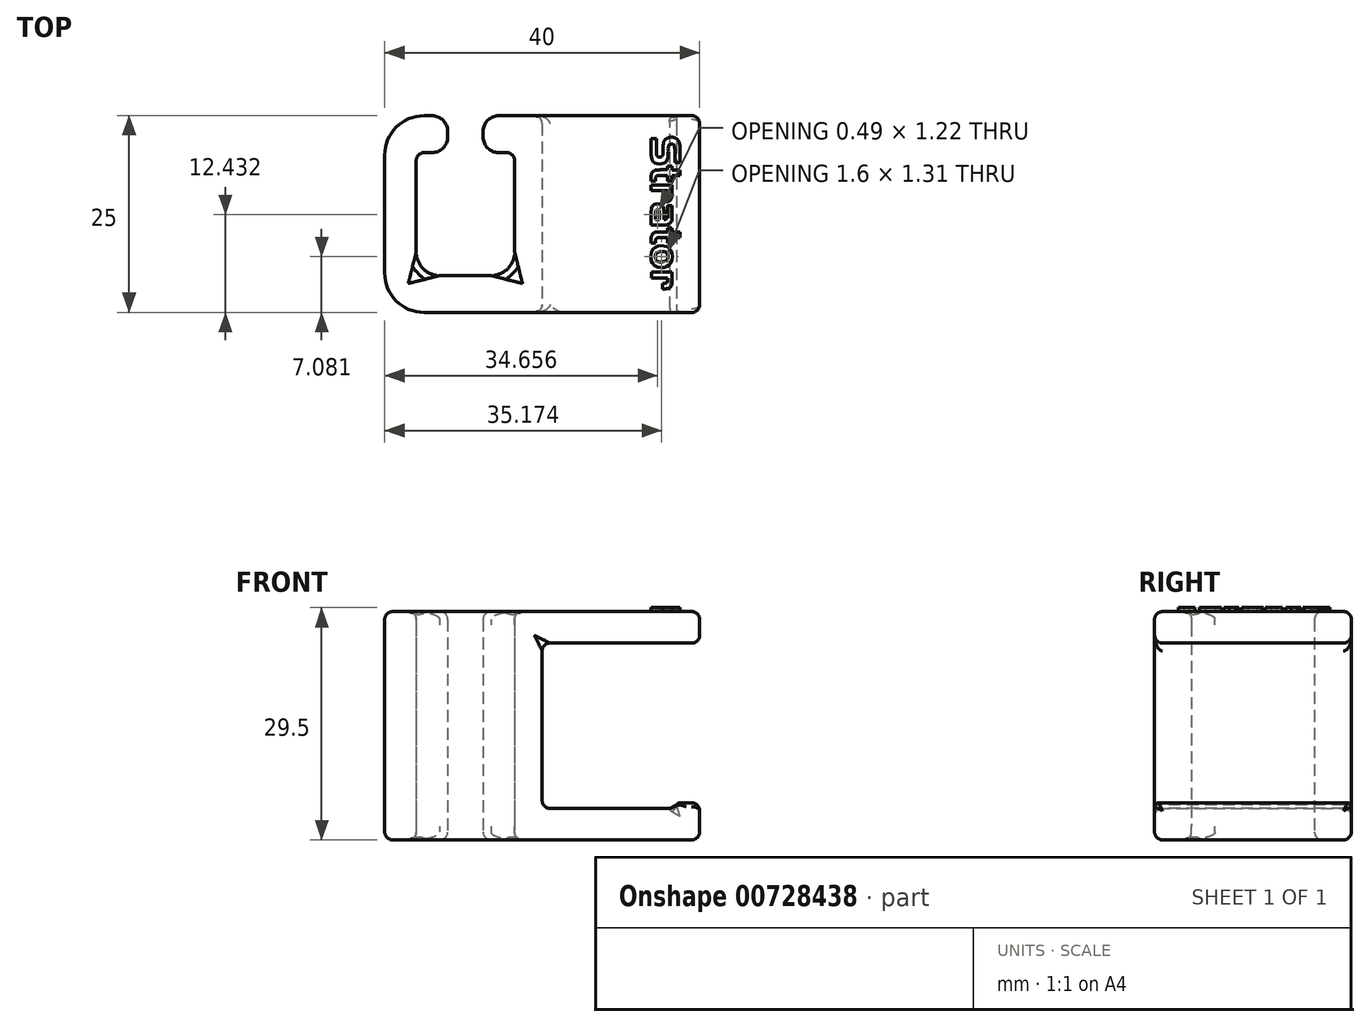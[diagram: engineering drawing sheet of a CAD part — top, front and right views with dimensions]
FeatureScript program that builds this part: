
annotation { "Feature Type Name" : "Feature", "Feature Type Description" : "" }
export const myFeature = defineFeature(function(context is Context, id is Id, definition is map)
    precondition{}
    {
        {
            var Q0;
            Q0=qCreatedBy(makeId("Top.planeOp"),FACE);
            var sketch = newSketch(context, id + "F0", { "sketchPlane" : qUnion([Q0])});
            skLineSegment(sketch, "E0", {"start": v(20, 11.92) * mm, "end": v(20, -13.08) * mm});
            skLineSegment(sketch, "E1", {"start": v(20, -13.08) * mm, "end": v(-20, -13.08) * mm});
            skLineSegment(sketch, "E2", {"start": v(-20, -13.08) * mm, "end": v(-20, 11.92) * mm});
            skLineSegment(sketch, "E3", {"start": v(-20, 11.92) * mm, "end": v(-12, 11.92) * mm});
            skLineSegment(sketch, "E4", {"start": v(-12, 11.92) * mm, "end": v(-12, 7.23) * mm});
            skLineSegment(sketch, "E5", {"start": v(-12, 7.23) * mm, "end": v(-16, 7.23) * mm});
            skLineSegment(sketch, "E6", {"start": v(-16, 7.23) * mm, "end": v(-16, -8.4) * mm});
            skLineSegment(sketch, "E7", {"start": v(-16, -8.4) * mm, "end": v(-3.5, -8.4) * mm});
            skLineSegment(sketch, "E8", {"start": v(-3.5, -8.4) * mm, "end": v(-3.5, 7.23) * mm});
            skLineSegment(sketch, "E9", {"start": v(-3.5, 7.23) * mm, "end": v(-7.5, 7.23) * mm});
            skLineSegment(sketch, "E10", {"start": v(-7.5, 7.23) * mm, "end": v(-7.5, 11.92) * mm});
            skLineSegment(sketch, "E11", {"start": v(-7.5, 11.92) * mm, "end": v(20, 11.92) * mm});
            skSolve(sketch);
        }
        {
            var Q0;
            Q0=makeQuery(id+"F0.imprint","IMPRINT",FACE,{"disambiguationData":[TD([[makeQuery(id+"F0.imprint","IMPRINT",EDGE,{"derivedFrom":sQuery(id+"F0.wireOp",EDGE,"E0")}),-1.0]])]});
            extrude(context, id + "F1", {"entities" : qUnion([Q0]), "depth" : 29 * mm, "offsetDistance" : 25 * mm});
        }
        {
            var Q0;
            Q0=qCreatedBy(makeId("Front.planeOp"),FACE);
            var sketch = newSketch(context, id + "F2", { "sketchPlane" : qUnion([Q0])});
            skLineSegment(sketch, "E12", {"start": v(0, 4) * mm, "end": v(0, 25) * mm});
            skLineSegment(sketch, "E13", {"start": v(0, 25) * mm, "end": v(36.44, 25) * mm});
            skLineSegment(sketch, "E14", {"start": v(36.44, 25) * mm, "end": v(36.44, 4.7) * mm});
            skLineSegment(sketch, "E15", {"start": v(36.44, 4.7) * mm, "end": v(17, 4.7) * mm});
            skLineSegment(sketch, "E16", {"start": v(17, 4.7) * mm, "end": v(17, 4) * mm});
            skLineSegment(sketch, "E17", {"start": v(17, 4) * mm, "end": v(0, 4) * mm});
            skLineSegment(sketch, "E18", {"start": v(26.72, 0) * mm, "end": v(26.72, 29) * mm, "construction": true});
            skPoint(sketch, "E18.startSnap0", {"position": v(26.72, 4.7) * mm});
            skSolve(sketch);
        }
        {
            var Q0;
            Q0=makeQuery(id+"F2.imprint","IMPRINT",FACE,{"disambiguationData":[TD([[makeQuery(id+"F2.imprint","IMPRINT",EDGE,{"derivedFrom":sQuery(id+"F2.wireOp",EDGE,"E12")}),-1.0]])]});
            extrude(context, id + "F3", {"entities" : qUnion([Q0]), "operationType" : NewBodyOperationType.REMOVE, "endBound" : BoundingType.THROUGH_ALL, "oppositeDirection" : true, "depth" : 25 * mm, "offsetDistance" : 25 * mm, "hasSecondDirection" : true, "secondDirectionOppositeDirection" : false, "secondDirectionDepth" : 25 * mm});
        }
        {
            var Q0;
            Q0=makeQuery(id+"F1.opExtrude","CAP_FACE",FACE,{"disambiguationData":[OSD([sQuery(id+"F0.wireOp",EDGE,"E0"),sQuery(id+"F0.wireOp",EDGE,"E1"),sQuery(id+"F0.wireOp",EDGE,"E2"),sQuery(id+"F0.wireOp",EDGE,"E3"),sQuery(id+"F0.wireOp",EDGE,"E4"),sQuery(id+"F0.wireOp",EDGE,"E5"),sQuery(id+"F0.wireOp",EDGE,"E6"),sQuery(id+"F0.wireOp",EDGE,"E7"),sQuery(id+"F0.wireOp",EDGE,"E8"),sQuery(id+"F0.wireOp",EDGE,"E9"),sQuery(id+"F0.wireOp",EDGE,"E10"),sQuery(id+"F0.wireOp",EDGE,"E11")])],"isStart":false});
            var Q1;
            Q1=makeQuery(id+"F1.opExtrude","SWEPT_EDGE",EDGE,{"disambiguationData":[OSD([sQuery(id+"F0.wireOp",EDGE,"E8"),sQuery(id+"F0.wireOp",EDGE,"E9")])]});
            var Q2;
            Q2=makeQuery(id+"F1.opExtrude","SWEPT_EDGE",EDGE,{"disambiguationData":[OSD([sQuery(id+"F0.wireOp",EDGE,"E5"),sQuery(id+"F0.wireOp",EDGE,"E6")])]});
            var Q3;
            Q3=makeQuery(id+"F1.opExtrude","CAP_EDGE",EDGE,{"disambiguationData":[OSD([sQuery(id+"F0.wireOp",EDGE,"E8")])],"isStart":true});
            var Q4;
            Q4=makeQuery(id+"F1.opExtrude","CAP_FACE",FACE,{"disambiguationData":[OSD([sQuery(id+"F0.wireOp",EDGE,"E0"),sQuery(id+"F0.wireOp",EDGE,"E1"),sQuery(id+"F0.wireOp",EDGE,"E2"),sQuery(id+"F0.wireOp",EDGE,"E3"),sQuery(id+"F0.wireOp",EDGE,"E4"),sQuery(id+"F0.wireOp",EDGE,"E5"),sQuery(id+"F0.wireOp",EDGE,"E6"),sQuery(id+"F0.wireOp",EDGE,"E7"),sQuery(id+"F0.wireOp",EDGE,"E8"),sQuery(id+"F0.wireOp",EDGE,"E9"),sQuery(id+"F0.wireOp",EDGE,"E10"),sQuery(id+"F0.wireOp",EDGE,"E11")])],"isStart":true});
            var Q5;
            Q5=makeQuery(id+"F3.boolean.opBoolean","INTERSECT",EDGE,{"derivedFrom":[makeQuery(id+"F1.opExtrude","SWEPT_FACE",FACE,{"disambiguationData":[OSD([sQuery(id+"F0.wireOp",EDGE,"E0")])]}),makeQuery(id+"F3.opExtrude","SWEPT_FACE",FACE,{"disambiguationData":[OSD([sQuery(id+"F2.wireOp",EDGE,"E15")])]})]});
            var Q6;
            Q6=makeQuery(id+"F3.boolean.opBoolean","INTERSECT",EDGE,{"derivedFrom":[makeQuery(id+"F1.opExtrude","SWEPT_FACE",FACE,{"disambiguationData":[OSD([sQuery(id+"F0.wireOp",EDGE,"E0")])]}),makeQuery(id+"F3.opExtrude","SWEPT_FACE",FACE,{"disambiguationData":[OSD([sQuery(id+"F2.wireOp",EDGE,"E13")])]})]});
            var Q7;
            Q7=makeQuery(id+"F3.boolean.opBoolean","INTERSECT",EDGE,{"derivedFrom":[makeQuery(id+"F1.opExtrude","SWEPT_FACE",FACE,{"disambiguationData":[OSD([sQuery(id+"F0.wireOp",EDGE,"E11")])]}),makeQuery(id+"F3.opExtrude","SWEPT_FACE",FACE,{"disambiguationData":[OSD([sQuery(id+"F2.wireOp",EDGE,"E13")])]})]});
            var Q8;
            {var subQ0=sQuery(id+"F0.wireOp",EDGE,"E0");var subQ1=sQuery(id+"F0.wireOp",EDGE,"E1");Q8=makeQuery(id+"F3.boolean.opBoolean","SPLIT",EDGE,{"disambiguationData":[TD([makeQuery(id+"F3.opExtrude","SWEPT_FACE",FACE,{"disambiguationData":[OSD([sQuery(id+"F2.wireOp",EDGE,"E15")])]})])],"derivedFrom":makeQuery(id+"F1.opExtrude","SWEPT_EDGE",EDGE,{"disambiguationData":[OSD([subQ0,subQ1])]})});}
            var Q9;
            Q9=makeQuery(id+"F3.boolean.opBoolean","COPY",EDGE,{"derivedFrom":makeQuery(id+"F3.opExtrude","SWEPT_EDGE",EDGE,{"disambiguationData":[OSD([sQuery(id+"F2.wireOp",EDGE,"E12"),sQuery(id+"F2.wireOp",EDGE,"E17")])]})});
            var Q10;
            Q10=makeQuery(id+"F3.boolean.opBoolean","INTERSECT",EDGE,{"derivedFrom":[makeQuery(id+"F1.opExtrude","SWEPT_FACE",FACE,{"disambiguationData":[OSD([sQuery(id+"F0.wireOp",EDGE,"E1")])]}),makeQuery(id+"F3.opExtrude","SWEPT_FACE",FACE,{"disambiguationData":[OSD([sQuery(id+"F2.wireOp",EDGE,"E13")])]})]});
            var Q11;
            Q11=makeQuery(id+"F3.boolean.opBoolean","INTERSECT",EDGE,{"derivedFrom":[makeQuery(id+"F1.opExtrude","SWEPT_FACE",FACE,{"disambiguationData":[OSD([sQuery(id+"F0.wireOp",EDGE,"E1")])]}),makeQuery(id+"F3.opExtrude","SWEPT_FACE",FACE,{"disambiguationData":[OSD([sQuery(id+"F2.wireOp",EDGE,"E12")])]})]});
            var Q12;
            {var subQ0=sQuery(id+"F0.wireOp",EDGE,"E0");var subQ1=sQuery(id+"F0.wireOp",EDGE,"E11");Q12=makeQuery(id+"F3.boolean.opBoolean","SPLIT",EDGE,{"disambiguationData":[TD([makeQuery(id+"F3.opExtrude","SWEPT_FACE",FACE,{"disambiguationData":[OSD([sQuery(id+"F2.wireOp",EDGE,"E15")])]})])],"derivedFrom":makeQuery(id+"F1.opExtrude","SWEPT_EDGE",EDGE,{"disambiguationData":[OSD([subQ0,subQ1])]})});}
            fillet(context, id + "F4", {"entities" : qUnion([Q0, Q1, Q2, Q3, Q4, Q5, Q6, Q7, Q8, Q9, Q10, Q11, Q12]), "radius" : 1 * mm, "tangentPropagation" : true, "allowEdgeOverflow" : false});
        }
        {
            var Q0;
            Q0=makeQuery(id+"F3.boolean.opBoolean","INTERSECT",EDGE,{"derivedFrom":[makeQuery(id+"F1.opExtrude","SWEPT_FACE",FACE,{"disambiguationData":[OSD([sQuery(id+"F0.wireOp",EDGE,"E11")])]}),makeQuery(id+"F3.opExtrude","SWEPT_FACE",FACE,{"disambiguationData":[OSD([sQuery(id+"F2.wireOp",EDGE,"E12")])]})]});
            fillet(context, id + "F5", {"entities" : qUnion([Q0]), "radius" : 1 * mm, "tangentPropagation" : true, "allowEdgeOverflow" : false});
        }
        {
            var Q0;
            Q0=makeQuery(id+"F3.boolean.opBoolean","COPY",EDGE,{"derivedFrom":makeQuery(id+"F3.opExtrude","SWEPT_EDGE",EDGE,{"disambiguationData":[OSD([sQuery(id+"F2.wireOp",EDGE,"E15"),sQuery(id+"F2.wireOp",EDGE,"E16")])]})});
            var Q1;
            Q1=makeQuery(id+"F3.boolean.opBoolean","INTERSECT",EDGE,{"derivedFrom":[makeQuery(id+"F1.opExtrude","SWEPT_FACE",FACE,{"disambiguationData":[OSD([sQuery(id+"F0.wireOp",EDGE,"E11")])]}),makeQuery(id+"F3.opExtrude","SWEPT_FACE",FACE,{"disambiguationData":[OSD([sQuery(id+"F2.wireOp",EDGE,"E15")])]})]});
            var Q2;
            Q2=makeQuery(id+"F3.boolean.opBoolean","INTERSECT",EDGE,{"derivedFrom":[makeQuery(id+"F1.opExtrude","SWEPT_FACE",FACE,{"disambiguationData":[OSD([sQuery(id+"F0.wireOp",EDGE,"E1")])]}),makeQuery(id+"F3.opExtrude","SWEPT_FACE",FACE,{"disambiguationData":[OSD([sQuery(id+"F2.wireOp",EDGE,"E15")])]})]});
            var Q3;
            Q3=makeQuery(id+"F3.boolean.opBoolean","INTERSECT",EDGE,{"derivedFrom":[makeQuery(id+"F1.opExtrude","SWEPT_FACE",FACE,{"disambiguationData":[OSD([sQuery(id+"F0.wireOp",EDGE,"E1")])]}),makeQuery(id+"F3.opExtrude","SWEPT_FACE",FACE,{"disambiguationData":[OSD([sQuery(id+"F2.wireOp",EDGE,"E16")])]})]});
            var Q4;
            Q4=makeQuery(id+"F3.boolean.opBoolean","INTERSECT",EDGE,{"derivedFrom":[makeQuery(id+"F1.opExtrude","SWEPT_FACE",FACE,{"disambiguationData":[OSD([sQuery(id+"F0.wireOp",EDGE,"E11")])]}),makeQuery(id+"F3.opExtrude","SWEPT_FACE",FACE,{"disambiguationData":[OSD([sQuery(id+"F2.wireOp",EDGE,"E16")])]})]});
            fillet(context, id + "F6", {"entities" : qUnion([Q0, Q1, Q2, Q3, Q4]), "radius" : 0.5 * mm, "tangentPropagation" : true, "allowEdgeOverflow" : false});
        }
        {
            var Q0;
            {var subQ0=sQuery(id+"F2.wireOp",EDGE,"E16");Q0=makeQuery(id+"F6.opFillet","BLEND_EDGE",EDGE,{"blendedFrom":[makeQuery(id+"F3.boolean.opBoolean","COPY",EDGE,{"derivedFrom":makeQuery(id+"F3.opExtrude","SWEPT_EDGE",EDGE,{"disambiguationData":[OSD([sQuery(id+"F2.wireOp",EDGE,"E15"),subQ0])]})}),makeQuery(id+"F3.boolean.opBoolean","COPY",FACE,{"derivedFrom":makeQuery(id+"F3.opExtrude","SWEPT_FACE",FACE,{"disambiguationData":[OSD([subQ0])]})})],"blendedInto":[makeQuery(id+"F3.boolean.opBoolean","COPY",FACE,{"derivedFrom":makeQuery(id+"F3.opExtrude","SWEPT_FACE",FACE,{"disambiguationData":[OSD([subQ0])]})})]});}
            var Q1;
            Q1=makeQuery(id+"F3.boolean.opBoolean","COPY",EDGE,{"derivedFrom":makeQuery(id+"F3.opExtrude","SWEPT_EDGE",EDGE,{"disambiguationData":[OSD([sQuery(id+"F2.wireOp",EDGE,"E16"),sQuery(id+"F2.wireOp",EDGE,"E17")])]})});
            chamfer(context, id + "F7", {"entities" : qUnion([Q0, Q1]), "width" : 1 * mm, "tangentPropagation" : true});
        }
        {
            var Q0;
            Q0=makeQuery(id+"F1.opExtrude","SWEPT_EDGE",EDGE,{"disambiguationData":[OSD([sQuery(id+"F0.wireOp",EDGE,"E1"),sQuery(id+"F0.wireOp",EDGE,"E2")])]});
            fillet(context, id + "F8", {"entities" : qUnion([Q0]), "radius" : 5 * mm, "tangentPropagation" : true, "allowEdgeOverflow" : false});
        }
        {
            var Q0;
            Q0=makeQuery(id+"F1.opExtrude","SWEPT_EDGE",EDGE,{"disambiguationData":[OSD([sQuery(id+"F0.wireOp",EDGE,"E2"),sQuery(id+"F0.wireOp",EDGE,"E3")])]});
            fillet(context, id + "F9", {"entities" : qUnion([Q0]), "radius" : 5 * mm, "tangentPropagation" : true, "allowEdgeOverflow" : false});
        }
        {
            var Q0;
            Q0=makeQuery(id+"F1.opExtrude","SWEPT_EDGE",EDGE,{"disambiguationData":[OSD([sQuery(id+"F0.wireOp",EDGE,"E7"),sQuery(id+"F0.wireOp",EDGE,"E8")])]});
            var Q1;
            Q1=makeQuery(id+"F1.opExtrude","SWEPT_EDGE",EDGE,{"disambiguationData":[OSD([sQuery(id+"F0.wireOp",EDGE,"E6"),sQuery(id+"F0.wireOp",EDGE,"E7")])]});
            fillet(context, id + "F10", {"entities" : qUnion([Q0, Q1]), "radius" : 3 * mm, "tangentPropagation" : true, "allowEdgeOverflow" : false});
        }
        {
            var Q0;
            Q0=makeQuery(id+"F3.boolean.opBoolean","COPY",FACE,{"derivedFrom":makeQuery(id+"F3.opExtrude","SWEPT_FACE",FACE,{"disambiguationData":[OSD([sQuery(id+"F2.wireOp",EDGE,"E13")])]})});
            fillet(context, id + "F11", {"entities" : qUnion([Q0]), "radius" : 1 * mm, "tangentPropagation" : true, "allowEdgeOverflow" : false});
        }
        {
            var Q0;
            {var subQ0=sQuery(id+"F0.wireOp",EDGE,"E0");var subQ1=sQuery(id+"F0.wireOp",EDGE,"E11");Q0=makeQuery(id+"F3.boolean.opBoolean","SPLIT",EDGE,{"disambiguationData":[TD([makeQuery(id+"F3.opExtrude","SWEPT_FACE",FACE,{"disambiguationData":[OSD([sQuery(id+"F2.wireOp",EDGE,"E13")])]})])],"derivedFrom":makeQuery(id+"F1.opExtrude","SWEPT_EDGE",EDGE,{"disambiguationData":[OSD([subQ0,subQ1])]})});}
            var Q1;
            {var subQ0=sQuery(id+"F0.wireOp",EDGE,"E0");var subQ1=sQuery(id+"F0.wireOp",EDGE,"E1");Q1=makeQuery(id+"F3.boolean.opBoolean","SPLIT",EDGE,{"disambiguationData":[TD([makeQuery(id+"F3.opExtrude","SWEPT_FACE",FACE,{"disambiguationData":[OSD([sQuery(id+"F2.wireOp",EDGE,"E13")])]})])],"derivedFrom":makeQuery(id+"F1.opExtrude","SWEPT_EDGE",EDGE,{"disambiguationData":[OSD([subQ0,subQ1])]})});}
            fillet(context, id + "F12", {"entities" : qUnion([Q0, Q1]), "radius" : 1 * mm, "tangentPropagation" : true, "allowEdgeOverflow" : false});
        }
        {
            var Q0;
            Q0=makeQuery(id+"F1.opExtrude","SWEPT_EDGE",EDGE,{"disambiguationData":[OSD([sQuery(id+"F0.wireOp",EDGE,"E9"),sQuery(id+"F0.wireOp",EDGE,"E10")])]});
            var Q1;
            Q1=makeQuery(id+"F1.opExtrude","SWEPT_EDGE",EDGE,{"disambiguationData":[OSD([sQuery(id+"F0.wireOp",EDGE,"E10"),sQuery(id+"F0.wireOp",EDGE,"E11")])]});
            var Q2;
            Q2=makeQuery(id+"F1.opExtrude","SWEPT_EDGE",EDGE,{"disambiguationData":[OSD([sQuery(id+"F0.wireOp",EDGE,"E3"),sQuery(id+"F0.wireOp",EDGE,"E4")])]});
            var Q3;
            Q3=makeQuery(id+"F1.opExtrude","SWEPT_EDGE",EDGE,{"disambiguationData":[OSD([sQuery(id+"F0.wireOp",EDGE,"E4"),sQuery(id+"F0.wireOp",EDGE,"E5")])]});
            fillet(context, id + "F13", {"entities" : qUnion([Q0, Q1, Q2, Q3]), "radius" : 2 * mm, "tangentPropagation" : true, "allowEdgeOverflow" : false});
        }
        {
            var Q0;
            Q0=qCreatedBy(makeId("Top.planeOp"),FACE);
            var sketch = newSketch(context, id + "F14", { "sketchPlane" : qUnion([Q0])});
            skLineSegment(sketch, "E19", {"start": v(22.35, 9) * mm, "end": v(23, 9) * mm});
            skLineSegment(sketch, "E20", {"start": v(23, 9) * mm, "end": v(23, 7.12) * mm});
            skLineSegment(sketch, "E21", {"start": v(23, 7.12) * mm, "end": v(23.03, 6.93) * mm});
            skLineSegment(sketch, "E22", {"start": v(23.03, 6.93) * mm, "end": v(23.06, 6.83) * mm});
            skLineSegment(sketch, "E23", {"start": v(23.06, 6.83) * mm, "end": v(23.1, 6.78) * mm});
            skLineSegment(sketch, "E24", {"start": v(23.1, 6.78) * mm, "end": v(23.12, 6.76) * mm});
            skLineSegment(sketch, "E25", {"start": v(23.12, 6.76) * mm, "end": v(23.15, 6.73) * mm});
            skLineSegment(sketch, "E26", {"start": v(23.15, 6.73) * mm, "end": v(23.2, 6.69) * mm});
            skLineSegment(sketch, "E27", {"start": v(23.2, 6.69) * mm, "end": v(23.25, 6.66) * mm});
            skLineSegment(sketch, "E28", {"start": v(23.25, 6.66) * mm, "end": v(23.32, 6.64) * mm});
            skLineSegment(sketch, "E29", {"start": v(23.32, 6.64) * mm, "end": v(23.4, 6.63) * mm});
            skLineSegment(sketch, "E30", {"start": v(23.4, 6.63) * mm, "end": v(23.47, 6.63) * mm});
            skLineSegment(sketch, "E31", {"start": v(23.47, 6.63) * mm, "end": v(23.53, 6.64) * mm});
            skLineSegment(sketch, "E32", {"start": v(23.53, 6.64) * mm, "end": v(23.62, 6.68) * mm});
            skLineSegment(sketch, "E33", {"start": v(23.62, 6.68) * mm, "end": v(23.68, 6.72) * mm});
            skLineSegment(sketch, "E34", {"start": v(23.68, 6.72) * mm, "end": v(23.71, 6.75) * mm});
            skLineSegment(sketch, "E35", {"start": v(23.71, 6.75) * mm, "end": v(23.75, 6.79) * mm});
            skLineSegment(sketch, "E36", {"start": v(23.75, 6.79) * mm, "end": v(23.79, 6.83) * mm});
            skLineSegment(sketch, "E37", {"start": v(23.79, 6.83) * mm, "end": v(23.82, 6.9) * mm});
            skLineSegment(sketch, "E38", {"start": v(23.82, 6.9) * mm, "end": v(23.84, 6.98) * mm});
            skLineSegment(sketch, "E39", {"start": v(23.84, 6.98) * mm, "end": v(23.86, 7.05) * mm});
            skLineSegment(sketch, "E40", {"start": v(23.86, 7.05) * mm, "end": v(23.87, 7.1) * mm});
            skLineSegment(sketch, "E41", {"start": v(23.87, 7.1) * mm, "end": v(23.88, 7.26) * mm});
            skLineSegment(sketch, "E42", {"start": v(23.88, 7.26) * mm, "end": v(23.88, 7.52) * mm});
            skLineSegment(sketch, "E43", {"start": v(23.88, 7.52) * mm, "end": v(23.88, 8.08) * mm});
            skLineSegment(sketch, "E44", {"start": v(23.88, 8.08) * mm, "end": v(23.88, 8.16) * mm});
            skLineSegment(sketch, "E45", {"start": v(23.88, 8.16) * mm, "end": v(23.9, 8.3) * mm});
            skLineSegment(sketch, "E46", {"start": v(23.9, 8.3) * mm, "end": v(23.9, 8.4) * mm});
            skLineSegment(sketch, "E47", {"start": v(23.9, 8.4) * mm, "end": v(23.92, 8.47) * mm});
            skLineSegment(sketch, "E48", {"start": v(23.92, 8.47) * mm, "end": v(23.94, 8.55) * mm});
            skLineSegment(sketch, "E49", {"start": v(23.94, 8.55) * mm, "end": v(23.97, 8.62) * mm});
            skLineSegment(sketch, "E50", {"start": v(23.97, 8.62) * mm, "end": v(24, 8.67) * mm});
            skLineSegment(sketch, "E51", {"start": v(24, 8.67) * mm, "end": v(24.02, 8.72) * mm});
            skLineSegment(sketch, "E52", {"start": v(24.02, 8.72) * mm, "end": v(24.05, 8.77) * mm});
            skLineSegment(sketch, "E53", {"start": v(24.05, 8.77) * mm, "end": v(24.08, 8.81) * mm});
            skLineSegment(sketch, "E54", {"start": v(24.08, 8.81) * mm, "end": v(24.13, 8.86) * mm});
            skLineSegment(sketch, "E55", {"start": v(24.13, 8.86) * mm, "end": v(24.18, 8.92) * mm});
            skLineSegment(sketch, "E56", {"start": v(24.18, 8.92) * mm, "end": v(24.23, 8.96) * mm});
            skLineSegment(sketch, "E57", {"start": v(24.23, 8.96) * mm, "end": v(24.28, 9) * mm});
            skLineSegment(sketch, "E58", {"start": v(24.28, 9) * mm, "end": v(24.33, 9.03) * mm});
            skLineSegment(sketch, "E59", {"start": v(24.33, 9.03) * mm, "end": v(24.4, 9.06) * mm});
            skLineSegment(sketch, "E60", {"start": v(24.4, 9.06) * mm, "end": v(24.45, 9.09) * mm});
            skLineSegment(sketch, "E61", {"start": v(24.45, 9.09) * mm, "end": v(24.5, 9.11) * mm});
            skLineSegment(sketch, "E62", {"start": v(24.5, 9.11) * mm, "end": v(24.58, 9.14) * mm});
            skLineSegment(sketch, "E63", {"start": v(24.58, 9.14) * mm, "end": v(24.66, 9.16) * mm});
            skLineSegment(sketch, "E64", {"start": v(24.66, 9.16) * mm, "end": v(24.74, 9.17) * mm});
            skLineSegment(sketch, "E65", {"start": v(24.74, 9.17) * mm, "end": v(24.82, 9.18) * mm});
            skLineSegment(sketch, "E66", {"start": v(24.82, 9.18) * mm, "end": v(24.88, 9.18) * mm});
            skLineSegment(sketch, "E67", {"start": v(24.88, 9.18) * mm, "end": v(25, 9.18) * mm});
            skLineSegment(sketch, "E68", {"start": v(25, 9.18) * mm, "end": v(25.1, 9.18) * mm});
            skLineSegment(sketch, "E69", {"start": v(25.1, 9.18) * mm, "end": v(25.21, 9.15) * mm});
            skLineSegment(sketch, "E70", {"start": v(25.21, 9.15) * mm, "end": v(25.3, 9.12) * mm});
            skLineSegment(sketch, "E71", {"start": v(25.3, 9.12) * mm, "end": v(25.38, 9.1) * mm});
            skLineSegment(sketch, "E72", {"start": v(25.38, 9.1) * mm, "end": v(25.48, 9.04) * mm});
            skLineSegment(sketch, "E73", {"start": v(25.48, 9.04) * mm, "end": v(25.56, 9) * mm});
            skLineSegment(sketch, "E74", {"start": v(25.56, 9) * mm, "end": v(25.62, 8.95) * mm});
            skLineSegment(sketch, "E75", {"start": v(25.62, 8.95) * mm, "end": v(25.68, 8.9) * mm});
            skLineSegment(sketch, "E76", {"start": v(25.68, 8.9) * mm, "end": v(25.76, 8.82) * mm});
            skLineSegment(sketch, "E77", {"start": v(25.76, 8.82) * mm, "end": v(25.79, 8.78) * mm});
            skLineSegment(sketch, "E78", {"start": v(25.79, 8.78) * mm, "end": v(25.84, 8.7) * mm});
            skLineSegment(sketch, "E79", {"start": v(25.84, 8.7) * mm, "end": v(25.88, 8.62) * mm});
            skLineSegment(sketch, "E80", {"start": v(25.88, 8.62) * mm, "end": v(25.9, 8.56) * mm});
            skLineSegment(sketch, "E81", {"start": v(25.9, 8.56) * mm, "end": v(25.93, 8.48) * mm});
            skLineSegment(sketch, "E82", {"start": v(25.93, 8.48) * mm, "end": v(25.95, 8.42) * mm});
            skLineSegment(sketch, "E83", {"start": v(25.95, 8.42) * mm, "end": v(25.96, 8.34) * mm});
            skLineSegment(sketch, "E84", {"start": v(25.96, 8.34) * mm, "end": v(25.97, 8.25) * mm});
            skLineSegment(sketch, "E85", {"start": v(25.97, 8.25) * mm, "end": v(25.98, 8.17) * mm});
            skLineSegment(sketch, "E86", {"start": v(25.98, 8.17) * mm, "end": v(25.98, 7.91) * mm});
            skLineSegment(sketch, "E87", {"start": v(25.98, 7.91) * mm, "end": v(25.99, 7.7) * mm});
            skLineSegment(sketch, "E88", {"start": v(25.99, 7.7) * mm, "end": v(25.99, 7.5) * mm});
            skLineSegment(sketch, "E89", {"start": v(25.99, 7.5) * mm, "end": v(25.99, 7.34) * mm});
            skLineSegment(sketch, "E90", {"start": v(25.99, 7.34) * mm, "end": v(25.99, 7.16) * mm});
            skLineSegment(sketch, "E91", {"start": v(25.99, 7.16) * mm, "end": v(25.99, 6.85) * mm});
            skLineSegment(sketch, "E92", {"start": v(25.99, 6.85) * mm, "end": v(25.99, 6.5) * mm});
            skLineSegment(sketch, "E93", {"start": v(25.99, 6.5) * mm, "end": v(25.99, 6.31) * mm});
            skLineSegment(sketch, "E94", {"start": v(25.99, 6.31) * mm, "end": v(25.99, 5.97) * mm});
            skLineSegment(sketch, "E95", {"start": v(25.99, 5.97) * mm, "end": v(25.35, 5.97) * mm});
            skLineSegment(sketch, "E96", {"start": v(25.35, 5.97) * mm, "end": v(25.35, 7.6) * mm});
            skLineSegment(sketch, "E97", {"start": v(25.35, 7.6) * mm, "end": v(25.34, 7.7) * mm});
            skLineSegment(sketch, "E98", {"start": v(25.34, 7.7) * mm, "end": v(25.34, 7.83) * mm});
            skLineSegment(sketch, "E99", {"start": v(25.34, 7.83) * mm, "end": v(25.33, 7.93) * mm});
            skLineSegment(sketch, "E100", {"start": v(25.33, 7.93) * mm, "end": v(25.33, 8.01) * mm});
            skLineSegment(sketch, "E101", {"start": v(25.33, 8.01) * mm, "end": v(25.31, 8.06) * mm});
            skLineSegment(sketch, "E102", {"start": v(25.31, 8.06) * mm, "end": v(25.3, 8.12) * mm});
            skLineSegment(sketch, "E103", {"start": v(25.3, 8.12) * mm, "end": v(25.27, 8.17) * mm});
            skLineSegment(sketch, "E104", {"start": v(25.27, 8.17) * mm, "end": v(25.24, 8.21) * mm});
            skLineSegment(sketch, "E105", {"start": v(25.24, 8.21) * mm, "end": v(25.2, 8.25) * mm});
            skLineSegment(sketch, "E106", {"start": v(25.2, 8.25) * mm, "end": v(25.13, 8.3) * mm});
            skFitSpline(sketch, "E107", {"points": [v(25.13, 8.3) * mm, v(25.03, 8.32) * mm, v(24.8, 8.32) * mm, v(24.7, 8.27) * mm, v(24.63, 8.2) * mm, v(24.55, 8.06) * mm, v(24.51, 7.86) * mm, v(24.51, 7.64) * mm, v(24.52, 7.28) * mm, v(24.5, 6.98) * mm, v(24.5, 6.74) * mm, v(24.44, 6.43) * mm, v(24.3, 6.13) * mm, v(24.12, 5.97) * mm, v(23.86, 5.84) * mm, v(23.55, 5.78) * mm, v(23.16, 5.8) * mm, v(22.83, 5.92) * mm, v(22.58, 6.1) * mm, v(22.43, 6.37) * mm, v(22.37, 6.7) * mm, v(22.36, 7.1) * mm, v(22.35, 9) * mm], "startDerivative": vector(-3.1, 1.34) * mm, "endDerivative": vector(-0.22, 17.05) * mm});
            skLineSegment(sketch, "E108", {"start": v(25, 5.5) * mm, "end": v(25, 5.04) * mm});
            skLineSegment(sketch, "E109", {"start": v(25, 5.04) * mm, "end": v(25.99, 5.04) * mm});
            skLineSegment(sketch, "E110", {"start": v(25.99, 5.04) * mm, "end": v(25.99, 4.3) * mm});
            skLineSegment(sketch, "E111", {"start": v(25.99, 4.3) * mm, "end": v(25, 4.3) * mm});
            skLineSegment(sketch, "E112", {"start": v(25, 4.3) * mm, "end": v(25, 3.62) * mm});
            skLineSegment(sketch, "E113", {"start": v(25, 3.62) * mm, "end": v(24.45, 3.62) * mm});
            skLineSegment(sketch, "E114", {"start": v(24.45, 3.62) * mm, "end": v(24.45, 4.3) * mm});
            skLineSegment(sketch, "E115", {"start": v(25, 5.5) * mm, "end": v(24.45, 5.5) * mm});
            skLineSegment(sketch, "E116", {"start": v(24.45, 5.5) * mm, "end": v(24.45, 5.04) * mm});
            skLineSegment(sketch, "E117", {"start": v(24.45, 4.3) * mm, "end": v(23.5, 4.3) * mm});
            skFitSpline(sketch, "E118", {"points": [v(23.5, 4.3) * mm, v(23.25, 4.3) * mm], "startDerivative": vector(-0.29, 0) * mm, "endDerivative": vector(-0.3, 0) * mm});
            skFitSpline(sketch, "E119", {"points": [v(23.25, 4.3) * mm, v(23.06, 4.26) * mm, v(22.96, 4.17) * mm, v(22.92, 4.04) * mm, v(22.91, 3.63) * mm], "startDerivative": vector(-0.9, -0.08) * mm, "endDerivative": vector(0.02, -1.29) * mm});
            skLineSegment(sketch, "E120", {"start": v(22.91, 3.63) * mm, "end": v(22.35, 3.63) * mm});
            skFitSpline(sketch, "E121", {"points": [v(22.35, 3.63) * mm, v(22.35, 4.33) * mm, v(22.39, 4.51) * mm, v(22.46, 4.7) * mm, v(22.6, 4.84) * mm, v(22.74, 4.95) * mm, v(22.96, 5.01) * mm, v(23.38, 5.04) * mm, v(24.45, 5.04) * mm], "startDerivative": vector(-0.1, 4.62) * mm, "endDerivative": vector(5.43, 0) * mm});
            skLineSegment(sketch, "E122", {"start": v(25, -2.4) * mm, "end": v(25, -2.85) * mm});
            skLineSegment(sketch, "E123", {"start": v(25, -2.85) * mm, "end": v(25.98, -2.85) * mm});
            skLineSegment(sketch, "E124", {"start": v(25.98, -2.85) * mm, "end": v(25.98, -3.59) * mm});
            skLineSegment(sketch, "E125", {"start": v(25.98, -3.59) * mm, "end": v(25, -3.59) * mm});
            skLineSegment(sketch, "E126", {"start": v(25, -3.59) * mm, "end": v(25, -4.27) * mm});
            skLineSegment(sketch, "E127", {"start": v(25, -4.27) * mm, "end": v(24.44, -4.27) * mm});
            skLineSegment(sketch, "E128", {"start": v(24.44, -4.27) * mm, "end": v(24.44, -3.59) * mm});
            skLineSegment(sketch, "E129", {"start": v(25, -2.4) * mm, "end": v(24.44, -2.4) * mm});
            skLineSegment(sketch, "E130", {"start": v(24.44, -2.4) * mm, "end": v(24.44, -2.84) * mm});
            skLineSegment(sketch, "E131", {"start": v(24.44, -3.59) * mm, "end": v(23.5, -3.59) * mm});
            skFitSpline(sketch, "E132", {"points": [v(23.5, -3.59) * mm, v(23.24, -3.59) * mm], "startDerivative": vector(-0.29, 0) * mm, "endDerivative": vector(-0.3, 0) * mm});
            skFitSpline(sketch, "E133", {"points": [v(23.24, -3.59) * mm, v(23.06, -3.63) * mm, v(22.96, -3.72) * mm, v(22.91, -3.85) * mm, v(22.9, -4.26) * mm], "startDerivative": vector(-0.9, -0.08) * mm, "endDerivative": vector(0.02, -1.29) * mm});
            skLineSegment(sketch, "E134", {"start": v(22.9, -4.26) * mm, "end": v(22.35, -4.26) * mm});
            skFitSpline(sketch, "E135", {"points": [v(22.35, -4.26) * mm, v(22.35, -3.56) * mm, v(22.38, -3.37) * mm, v(22.46, -3.2) * mm, v(22.59, -3.05) * mm, v(22.73, -2.94) * mm, v(22.95, -2.88) * mm, v(23.37, -2.85) * mm, v(24.44, -2.84) * mm], "startDerivative": vector(-0.1, 4.62) * mm, "endDerivative": vector(5.43, 0) * mm});
            skLineSegment(sketch, "E136", {"start": v(22.35, 2.4) * mm, "end": v(22.35, 3.12) * mm});
            skLineSegment(sketch, "E137", {"start": v(22.35, 3.12) * mm, "end": v(25, 3.12) * mm});
            skLineSegment(sketch, "E138", {"start": v(22.35, 2.4) * mm, "end": v(24.44, 2.4) * mm});
            skLineSegment(sketch, "E139", {"start": v(23.8, 1.7) * mm, "end": v(23.8, 1) * mm});
            skFitSpline(sketch, "E140", {"points": [v(24.44, 2.4) * mm, v(24.44, 2.16) * mm, v(24.43, 2) * mm, v(24.4, 1.91) * mm, v(24.36, 1.83) * mm, v(24.28, 1.76) * mm, v(24.16, 1.72) * mm, v(24.03, 1.71) * mm, v(23.8, 1.7) * mm], "startDerivative": vector(0, -1.5) * mm, "endDerivative": vector(-1.54, -0.02) * mm});
            skFitSpline(sketch, "E141", {"points": [v(25, 3.12) * mm, v(25, 2.03) * mm, v(25, 1.72) * mm, v(24.97, 1.56) * mm, v(24.94, 1.45) * mm, v(24.87, 1.31) * mm, v(24.69, 1.12) * mm, v(24.42, 1.03) * mm, v(23.8, 1) * mm], "startDerivative": vector(0, -5.47) * mm, "endDerivative": vector(-4.03, -0.06) * mm});
            skLineSegment(sketch, "E142", {"start": v(22.36, -8.7) * mm, "end": v(22.36, -7.97) * mm});
            skLineSegment(sketch, "E143", {"start": v(22.36, -7.97) * mm, "end": v(25, -7.97) * mm});
            skLineSegment(sketch, "E144", {"start": v(22.36, -8.7) * mm, "end": v(24.44, -8.7) * mm});
            skLineSegment(sketch, "E145", {"start": v(23.81, -9.38) * mm, "end": v(23.81, -10.08) * mm});
            skFitSpline(sketch, "E146", {"points": [v(24.44, -8.7) * mm, v(24.44, -8.93) * mm, v(24.44, -9.08) * mm, v(24.41, -9.18) * mm, v(24.37, -9.26) * mm, v(24.28, -9.33) * mm, v(24.16, -9.37) * mm, v(24.04, -9.38) * mm, v(23.81, -9.38) * mm], "startDerivative": vector(0, -1.5) * mm, "endDerivative": vector(-1.54, -0.02) * mm});
            skFitSpline(sketch, "E147", {"points": [v(25, -7.97) * mm, v(25, -9.06) * mm, v(25, -9.37) * mm, v(24.97, -9.53) * mm, v(24.94, -9.64) * mm, v(24.88, -9.78) * mm, v(24.7, -9.97) * mm, v(24.43, -10.06) * mm, v(23.81, -10.08) * mm], "startDerivative": vector(0, -5.47) * mm, "endDerivative": vector(-4.03, -0.06) * mm});
            skFitSpline(sketch, "E148", {"points": [v(24.47, -5.88) * mm, v(24.44, -6.27) * mm, v(24.2, -6.55) * mm, v(23.7, -6.66) * mm, v(23.18, -6.57) * mm, v(22.9, -6.23) * mm, v(22.88, -5.98) * mm, v(22.92, -5.7) * mm, v(23.17, -5.45) * mm, v(23.5, -5.35) * mm, v(24.02, -5.38) * mm, v(24.36, -5.59) * mm, v(24.47, -5.88) * mm]});
            skFitSpline(sketch, "E149", {"points": [v(25.04, -5.98) * mm, v(24.87, -6.78) * mm, v(24.32, -7.26) * mm, v(23.68, -7.4) * mm, v(22.75, -7.1) * mm, v(22.37, -6.53) * mm, v(22.3, -5.91) * mm, v(22.46, -5.2) * mm, v(22.97, -4.74) * mm, v(23.7, -4.6) * mm, v(24.44, -4.78) * mm, v(24.86, -5.25) * mm, v(25.04, -5.98) * mm]});
            skLineSegment(sketch, "E150", {"start": v(22.91, -1.26) * mm, "end": v(23.4, -1.26) * mm});
            skLineSegment(sketch, "E151", {"start": v(25, 0.53) * mm, "end": v(24.44, 0.53) * mm});
            skFitSpline(sketch, "E152", {"points": [v(24.44, 0.53) * mm, v(24.44, -0.7) * mm, v(24.4, -1) * mm, v(24.35, -1.14) * mm, v(24.2, -1.25) * mm, v(23.96, -1.26) * mm], "startDerivative": vector(0.06, -3.81) * mm, "endDerivative": vector(-1.46, 0.07) * mm});
            skFitSpline(sketch, "E153", {"points": [v(23.96, -1.26) * mm, v(23.96, -0.27) * mm, v(23.9, 0.22) * mm, v(23.75, 0.47) * mm, v(23.46, 0.66) * mm, v(23.13, 0.72) * mm, v(22.74, 0.63) * mm, v(22.45, 0.36) * mm, v(22.36, -0.07) * mm, v(22.35, -1.99) * mm], "startDerivative": vector(0.08, 7.18) * mm, "endDerivative": vector(0.06, -10.92) * mm});
            skFitSpline(sketch, "E154", {"points": [v(23.4, -1.26) * mm, v(23.4, -0.33) * mm, v(23.35, -0.11) * mm, v(23.15, -0.02) * mm, v(22.99, -0.08) * mm, v(22.91, -1.26) * mm], "startDerivative": vector(0.07, 8.92) * mm, "endDerivative": vector(0.03, -8.43) * mm});
            skFitSpline(sketch, "E155", {"points": [v(22.35, -1.99) * mm, v(24.12, -1.99) * mm, v(24.27, -1.97) * mm, v(24.45, -1.91) * mm, v(24.7, -1.76) * mm, v(24.94, -1.44) * mm, v(25, -0.94) * mm, v(25, -0.6) * mm, v(25, 0.53) * mm], "startDerivative": vector(9.7, -0.06) * mm, "endDerivative": vector(0.03, 7.02) * mm});
            skLineSegment(sketch, "E156", {"start": v(25.99, 13.53) * mm, "end": v(17.49, 13.53) * mm, "construction": true});
            skSolve(sketch);
        }
        {
            var Q0;
            Q0=makeQuery(id+"F14.imprint","IMPRINT",FACE,{"disambiguationData":[TD([[makeQuery(id+"F14.imprint","IMPRINT",EDGE,{"derivedFrom":sQuery(id+"F14.wireOp",EDGE,"E19")}),-1.0]])]});
            var Q1;
            Q1=makeQuery(id+"F14.imprint","IMPRINT",FACE,{"disambiguationData":[TD([[makeQuery(id+"F14.imprint","IMPRINT",EDGE,{"derivedFrom":sQuery(id+"F14.wireOp",EDGE,"E108")}),-1.0]])]});
            var Q2;
            Q2=makeQuery(id+"F14.imprint","IMPRINT",FACE,{"disambiguationData":[TD([[makeQuery(id+"F14.imprint","IMPRINT",EDGE,{"derivedFrom":sQuery(id+"F14.wireOp",EDGE,"E136")}),-1.0]])]});
            var Q3;
            Q3=makeQuery(id+"F14.imprint","IMPRINT",FACE,{"disambiguationData":[TD([[makeQuery(id+"F14.imprint","IMPRINT",EDGE,{"derivedFrom":sQuery(id+"F14.wireOp",EDGE,"E150")}),-1.0]])]});
            var Q4;
            Q4=makeQuery(id+"F14.imprint","IMPRINT",FACE,{"disambiguationData":[TD([[makeQuery(id+"F14.imprint","IMPRINT",EDGE,{"derivedFrom":sQuery(id+"F14.wireOp",EDGE,"E122")}),-1.0]])]});
            var Q5;
            Q5=makeQuery(id+"F14.imprint","IMPRINT",FACE,{"disambiguationData":[TD([[makeQuery(id+"F14.imprint","IMPRINT",EDGE,{"derivedFrom":sQuery(id+"F14.wireOp",EDGE,"E148")}),1.0]])]});
            var Q6;
            Q6=makeQuery(id+"F14.imprint","IMPRINT",FACE,{"disambiguationData":[TD([[makeQuery(id+"F14.imprint","IMPRINT",EDGE,{"derivedFrom":sQuery(id+"F14.wireOp",EDGE,"E142")}),-1.0]])]});
            extrude(context, id + "F15", {"entities" : qUnion([Q0, Q1, Q2, Q3, Q4, Q5, Q6]), "operationType" : NewBodyOperationType.ADD, "depth" : 0.5 * mm, "offsetDistance" : 25 * mm});
        }
        {
            var Q0;
            Q0=makeQuery(id+"F15.opExtrude","SWEPT_BODY",BODY,{"disambiguationData":[OSD([sQuery(id+"F14.wireOp",EDGE,"E148"),sQuery(id+"F14.wireOp",EDGE,"E149")])]});
            var Q1;
            Q1=makeQuery(id+"F15.opExtrude","SWEPT_BODY",BODY,{"disambiguationData":[OSD([sQuery(id+"F14.wireOp",EDGE,"E142"),sQuery(id+"F14.wireOp",EDGE,"E143"),sQuery(id+"F14.wireOp",EDGE,"E144"),sQuery(id+"F14.wireOp",EDGE,"E145"),sQuery(id+"F14.wireOp",EDGE,"E146"),sQuery(id+"F14.wireOp",EDGE,"E147")])]});
            var Q2;
            Q2=makeQuery(id+"F15.opExtrude","SWEPT_BODY",BODY,{"disambiguationData":[OSD([sQuery(id+"F14.wireOp",EDGE,"E150"),sQuery(id+"F14.wireOp",EDGE,"E151"),sQuery(id+"F14.wireOp",EDGE,"E152"),sQuery(id+"F14.wireOp",EDGE,"E153"),sQuery(id+"F14.wireOp",EDGE,"E154"),sQuery(id+"F14.wireOp",EDGE,"E155")])]});
            var Q3;
            Q3=makeQuery(id+"F15.opExtrude","SWEPT_BODY",BODY,{"disambiguationData":[OSD([sQuery(id+"F14.wireOp",EDGE,"E122"),sQuery(id+"F14.wireOp",EDGE,"E123"),sQuery(id+"F14.wireOp",EDGE,"E124"),sQuery(id+"F14.wireOp",EDGE,"E125"),sQuery(id+"F14.wireOp",EDGE,"E126"),sQuery(id+"F14.wireOp",EDGE,"E127"),sQuery(id+"F14.wireOp",EDGE,"E128"),sQuery(id+"F14.wireOp",EDGE,"E129"),sQuery(id+"F14.wireOp",EDGE,"E130"),sQuery(id+"F14.wireOp",EDGE,"E131"),sQuery(id+"F14.wireOp",EDGE,"E132"),sQuery(id+"F14.wireOp",EDGE,"E133"),sQuery(id+"F14.wireOp",EDGE,"E134"),sQuery(id+"F14.wireOp",EDGE,"E135")])]});
            var Q4;
            Q4=makeQuery(id+"F15.opExtrude","SWEPT_BODY",BODY,{"disambiguationData":[OSD([sQuery(id+"F14.wireOp",EDGE,"E136"),sQuery(id+"F14.wireOp",EDGE,"E137"),sQuery(id+"F14.wireOp",EDGE,"E138"),sQuery(id+"F14.wireOp",EDGE,"E139"),sQuery(id+"F14.wireOp",EDGE,"E140"),sQuery(id+"F14.wireOp",EDGE,"E141")])]});
            var Q5;
            Q5=makeQuery(id+"F15.opExtrude","SWEPT_BODY",BODY,{"disambiguationData":[OSD([sQuery(id+"F14.wireOp",EDGE,"E108"),sQuery(id+"F14.wireOp",EDGE,"E109"),sQuery(id+"F14.wireOp",EDGE,"E110"),sQuery(id+"F14.wireOp",EDGE,"E111"),sQuery(id+"F14.wireOp",EDGE,"E112"),sQuery(id+"F14.wireOp",EDGE,"E113"),sQuery(id+"F14.wireOp",EDGE,"E114"),sQuery(id+"F14.wireOp",EDGE,"E115"),sQuery(id+"F14.wireOp",EDGE,"E116"),sQuery(id+"F14.wireOp",EDGE,"E117"),sQuery(id+"F14.wireOp",EDGE,"E118"),sQuery(id+"F14.wireOp",EDGE,"E119"),sQuery(id+"F14.wireOp",EDGE,"E120"),sQuery(id+"F14.wireOp",EDGE,"E121")])]});
            var Q6;
            Q6=makeQuery(id+"F15.opExtrude","SWEPT_BODY",BODY,{"disambiguationData":[OSD([sQuery(id+"F14.wireOp",EDGE,"E19"),sQuery(id+"F14.wireOp",EDGE,"E20"),sQuery(id+"F14.wireOp",EDGE,"E21"),sQuery(id+"F14.wireOp",EDGE,"E22"),sQuery(id+"F14.wireOp",EDGE,"E23"),sQuery(id+"F14.wireOp",EDGE,"E24"),sQuery(id+"F14.wireOp",EDGE,"E25"),sQuery(id+"F14.wireOp",EDGE,"E26"),sQuery(id+"F14.wireOp",EDGE,"E27"),sQuery(id+"F14.wireOp",EDGE,"E28"),sQuery(id+"F14.wireOp",EDGE,"E29"),sQuery(id+"F14.wireOp",EDGE,"E30"),sQuery(id+"F14.wireOp",EDGE,"E31"),sQuery(id+"F14.wireOp",EDGE,"E32"),sQuery(id+"F14.wireOp",EDGE,"E33"),sQuery(id+"F14.wireOp",EDGE,"E34"),sQuery(id+"F14.wireOp",EDGE,"E35"),sQuery(id+"F14.wireOp",EDGE,"E36"),sQuery(id+"F14.wireOp",EDGE,"E37"),sQuery(id+"F14.wireOp",EDGE,"E38"),sQuery(id+"F14.wireOp",EDGE,"E39"),sQuery(id+"F14.wireOp",EDGE,"E40"),sQuery(id+"F14.wireOp",EDGE,"E41"),sQuery(id+"F14.wireOp",EDGE,"E42"),sQuery(id+"F14.wireOp",EDGE,"E43"),sQuery(id+"F14.wireOp",EDGE,"E44"),sQuery(id+"F14.wireOp",EDGE,"E45"),sQuery(id+"F14.wireOp",EDGE,"E46"),sQuery(id+"F14.wireOp",EDGE,"E47"),sQuery(id+"F14.wireOp",EDGE,"E48"),sQuery(id+"F14.wireOp",EDGE,"E49"),sQuery(id+"F14.wireOp",EDGE,"E50"),sQuery(id+"F14.wireOp",EDGE,"E51"),sQuery(id+"F14.wireOp",EDGE,"E52"),sQuery(id+"F14.wireOp",EDGE,"E53"),sQuery(id+"F14.wireOp",EDGE,"E54"),sQuery(id+"F14.wireOp",EDGE,"E55"),sQuery(id+"F14.wireOp",EDGE,"E56"),sQuery(id+"F14.wireOp",EDGE,"E57"),sQuery(id+"F14.wireOp",EDGE,"E58"),sQuery(id+"F14.wireOp",EDGE,"E59"),sQuery(id+"F14.wireOp",EDGE,"E60"),sQuery(id+"F14.wireOp",EDGE,"E61"),sQuery(id+"F14.wireOp",EDGE,"E62"),sQuery(id+"F14.wireOp",EDGE,"E63"),sQuery(id+"F14.wireOp",EDGE,"E64"),sQuery(id+"F14.wireOp",EDGE,"E65"),sQuery(id+"F14.wireOp",EDGE,"E66"),sQuery(id+"F14.wireOp",EDGE,"E67"),sQuery(id+"F14.wireOp",EDGE,"E68"),sQuery(id+"F14.wireOp",EDGE,"E69"),sQuery(id+"F14.wireOp",EDGE,"E70"),sQuery(id+"F14.wireOp",EDGE,"E71"),sQuery(id+"F14.wireOp",EDGE,"E72"),sQuery(id+"F14.wireOp",EDGE,"E73"),sQuery(id+"F14.wireOp",EDGE,"E74"),sQuery(id+"F14.wireOp",EDGE,"E75"),sQuery(id+"F14.wireOp",EDGE,"E76"),sQuery(id+"F14.wireOp",EDGE,"E77"),sQuery(id+"F14.wireOp",EDGE,"E78"),sQuery(id+"F14.wireOp",EDGE,"E79"),sQuery(id+"F14.wireOp",EDGE,"E80"),sQuery(id+"F14.wireOp",EDGE,"E81"),sQuery(id+"F14.wireOp",EDGE,"E82"),sQuery(id+"F14.wireOp",EDGE,"E83"),sQuery(id+"F14.wireOp",EDGE,"E84"),sQuery(id+"F14.wireOp",EDGE,"E85"),sQuery(id+"F14.wireOp",EDGE,"E86"),sQuery(id+"F14.wireOp",EDGE,"E87"),sQuery(id+"F14.wireOp",EDGE,"E88"),sQuery(id+"F14.wireOp",EDGE,"E89"),sQuery(id+"F14.wireOp",EDGE,"E90"),sQuery(id+"F14.wireOp",EDGE,"E91"),sQuery(id+"F14.wireOp",EDGE,"E92"),sQuery(id+"F14.wireOp",EDGE,"E93"),sQuery(id+"F14.wireOp",EDGE,"E94"),sQuery(id+"F14.wireOp",EDGE,"E95"),sQuery(id+"F14.wireOp",EDGE,"E96"),sQuery(id+"F14.wireOp",EDGE,"E97"),sQuery(id+"F14.wireOp",EDGE,"E98"),sQuery(id+"F14.wireOp",EDGE,"E99"),sQuery(id+"F14.wireOp",EDGE,"E100"),sQuery(id+"F14.wireOp",EDGE,"E101"),sQuery(id+"F14.wireOp",EDGE,"E102"),sQuery(id+"F14.wireOp",EDGE,"E103"),sQuery(id+"F14.wireOp",EDGE,"E104"),sQuery(id+"F14.wireOp",EDGE,"E105"),sQuery(id+"F14.wireOp",EDGE,"E106"),sQuery(id+"F14.wireOp",EDGE,"E107")])]});
            var Q7;
            Q7=sQuery(id+"F2.wireOp",EDGE,"E18");
            transform(context, id + "F16", {"entities" : qUnion([Q0, Q1, Q2, Q3, Q4, Q5, Q6]), "transformType" : TransformType.TRANSLATION_ENTITY, "oppositeDirectionEntity" : false, "transformLine" : qUnion([Q7]), "makeCopy" : false});
        }
        {
            var Q0;
            Q0=sQuery(id+"F14.wireOp",EDGE,"E156");
            cPoint(context, id + "F17", {"entities" : qUnion([Q0]), "parameter" : 0.5});
        }
        {
            var Q0;
            Q0=makeQuery(id+"F15.opExtrude","SWEPT_BODY",BODY,{"disambiguationData":[OSD([sQuery(id+"F14.wireOp",EDGE,"E19"),sQuery(id+"F14.wireOp",EDGE,"E20"),sQuery(id+"F14.wireOp",EDGE,"E21"),sQuery(id+"F14.wireOp",EDGE,"E22"),sQuery(id+"F14.wireOp",EDGE,"E23"),sQuery(id+"F14.wireOp",EDGE,"E24"),sQuery(id+"F14.wireOp",EDGE,"E25"),sQuery(id+"F14.wireOp",EDGE,"E26"),sQuery(id+"F14.wireOp",EDGE,"E27"),sQuery(id+"F14.wireOp",EDGE,"E28"),sQuery(id+"F14.wireOp",EDGE,"E29"),sQuery(id+"F14.wireOp",EDGE,"E30"),sQuery(id+"F14.wireOp",EDGE,"E31"),sQuery(id+"F14.wireOp",EDGE,"E32"),sQuery(id+"F14.wireOp",EDGE,"E33"),sQuery(id+"F14.wireOp",EDGE,"E34"),sQuery(id+"F14.wireOp",EDGE,"E35"),sQuery(id+"F14.wireOp",EDGE,"E36"),sQuery(id+"F14.wireOp",EDGE,"E37"),sQuery(id+"F14.wireOp",EDGE,"E38"),sQuery(id+"F14.wireOp",EDGE,"E39"),sQuery(id+"F14.wireOp",EDGE,"E40"),sQuery(id+"F14.wireOp",EDGE,"E41"),sQuery(id+"F14.wireOp",EDGE,"E42"),sQuery(id+"F14.wireOp",EDGE,"E43"),sQuery(id+"F14.wireOp",EDGE,"E44"),sQuery(id+"F14.wireOp",EDGE,"E45"),sQuery(id+"F14.wireOp",EDGE,"E46"),sQuery(id+"F14.wireOp",EDGE,"E47"),sQuery(id+"F14.wireOp",EDGE,"E48"),sQuery(id+"F14.wireOp",EDGE,"E49"),sQuery(id+"F14.wireOp",EDGE,"E50"),sQuery(id+"F14.wireOp",EDGE,"E51"),sQuery(id+"F14.wireOp",EDGE,"E52"),sQuery(id+"F14.wireOp",EDGE,"E53"),sQuery(id+"F14.wireOp",EDGE,"E54"),sQuery(id+"F14.wireOp",EDGE,"E55"),sQuery(id+"F14.wireOp",EDGE,"E56"),sQuery(id+"F14.wireOp",EDGE,"E57"),sQuery(id+"F14.wireOp",EDGE,"E58"),sQuery(id+"F14.wireOp",EDGE,"E59"),sQuery(id+"F14.wireOp",EDGE,"E60"),sQuery(id+"F14.wireOp",EDGE,"E61"),sQuery(id+"F14.wireOp",EDGE,"E62"),sQuery(id+"F14.wireOp",EDGE,"E63"),sQuery(id+"F14.wireOp",EDGE,"E64"),sQuery(id+"F14.wireOp",EDGE,"E65"),sQuery(id+"F14.wireOp",EDGE,"E66"),sQuery(id+"F14.wireOp",EDGE,"E67"),sQuery(id+"F14.wireOp",EDGE,"E68"),sQuery(id+"F14.wireOp",EDGE,"E69"),sQuery(id+"F14.wireOp",EDGE,"E70"),sQuery(id+"F14.wireOp",EDGE,"E71"),sQuery(id+"F14.wireOp",EDGE,"E72"),sQuery(id+"F14.wireOp",EDGE,"E73"),sQuery(id+"F14.wireOp",EDGE,"E74"),sQuery(id+"F14.wireOp",EDGE,"E75"),sQuery(id+"F14.wireOp",EDGE,"E76"),sQuery(id+"F14.wireOp",EDGE,"E77"),sQuery(id+"F14.wireOp",EDGE,"E78"),sQuery(id+"F14.wireOp",EDGE,"E79"),sQuery(id+"F14.wireOp",EDGE,"E80"),sQuery(id+"F14.wireOp",EDGE,"E81"),sQuery(id+"F14.wireOp",EDGE,"E82"),sQuery(id+"F14.wireOp",EDGE,"E83"),sQuery(id+"F14.wireOp",EDGE,"E84"),sQuery(id+"F14.wireOp",EDGE,"E85"),sQuery(id+"F14.wireOp",EDGE,"E86"),sQuery(id+"F14.wireOp",EDGE,"E87"),sQuery(id+"F14.wireOp",EDGE,"E88"),sQuery(id+"F14.wireOp",EDGE,"E89"),sQuery(id+"F14.wireOp",EDGE,"E90"),sQuery(id+"F14.wireOp",EDGE,"E91"),sQuery(id+"F14.wireOp",EDGE,"E92"),sQuery(id+"F14.wireOp",EDGE,"E93"),sQuery(id+"F14.wireOp",EDGE,"E94"),sQuery(id+"F14.wireOp",EDGE,"E95"),sQuery(id+"F14.wireOp",EDGE,"E96"),sQuery(id+"F14.wireOp",EDGE,"E97"),sQuery(id+"F14.wireOp",EDGE,"E98"),sQuery(id+"F14.wireOp",EDGE,"E99"),sQuery(id+"F14.wireOp",EDGE,"E100"),sQuery(id+"F14.wireOp",EDGE,"E101"),sQuery(id+"F14.wireOp",EDGE,"E102"),sQuery(id+"F14.wireOp",EDGE,"E103"),sQuery(id+"F14.wireOp",EDGE,"E104"),sQuery(id+"F14.wireOp",EDGE,"E105"),sQuery(id+"F14.wireOp",EDGE,"E106"),sQuery(id+"F14.wireOp",EDGE,"E107")])]});
            var Q1;
            Q1=makeQuery(id+"F15.opExtrude","SWEPT_BODY",BODY,{"disambiguationData":[OSD([sQuery(id+"F14.wireOp",EDGE,"E150"),sQuery(id+"F14.wireOp",EDGE,"E151"),sQuery(id+"F14.wireOp",EDGE,"E152"),sQuery(id+"F14.wireOp",EDGE,"E153"),sQuery(id+"F14.wireOp",EDGE,"E154"),sQuery(id+"F14.wireOp",EDGE,"E155")])]});
            var Q2;
            Q2=makeQuery(id+"F15.opExtrude","SWEPT_BODY",BODY,{"disambiguationData":[OSD([sQuery(id+"F14.wireOp",EDGE,"E148"),sQuery(id+"F14.wireOp",EDGE,"E149")])]});
            var Q3;
            Q3=makeQuery(id+"F15.opExtrude","SWEPT_BODY",BODY,{"disambiguationData":[OSD([sQuery(id+"F14.wireOp",EDGE,"E142"),sQuery(id+"F14.wireOp",EDGE,"E143"),sQuery(id+"F14.wireOp",EDGE,"E144"),sQuery(id+"F14.wireOp",EDGE,"E145"),sQuery(id+"F14.wireOp",EDGE,"E146"),sQuery(id+"F14.wireOp",EDGE,"E147")])]});
            var Q4;
            Q4=makeQuery(id+"F15.opExtrude","SWEPT_BODY",BODY,{"disambiguationData":[OSD([sQuery(id+"F14.wireOp",EDGE,"E136"),sQuery(id+"F14.wireOp",EDGE,"E137"),sQuery(id+"F14.wireOp",EDGE,"E138"),sQuery(id+"F14.wireOp",EDGE,"E139"),sQuery(id+"F14.wireOp",EDGE,"E140"),sQuery(id+"F14.wireOp",EDGE,"E141")])]});
            var Q5;
            Q5=makeQuery(id+"F15.opExtrude","SWEPT_BODY",BODY,{"disambiguationData":[OSD([sQuery(id+"F14.wireOp",EDGE,"E108"),sQuery(id+"F14.wireOp",EDGE,"E109"),sQuery(id+"F14.wireOp",EDGE,"E110"),sQuery(id+"F14.wireOp",EDGE,"E111"),sQuery(id+"F14.wireOp",EDGE,"E112"),sQuery(id+"F14.wireOp",EDGE,"E113"),sQuery(id+"F14.wireOp",EDGE,"E114"),sQuery(id+"F14.wireOp",EDGE,"E115"),sQuery(id+"F14.wireOp",EDGE,"E116"),sQuery(id+"F14.wireOp",EDGE,"E117"),sQuery(id+"F14.wireOp",EDGE,"E118"),sQuery(id+"F14.wireOp",EDGE,"E119"),sQuery(id+"F14.wireOp",EDGE,"E120"),sQuery(id+"F14.wireOp",EDGE,"E121")])]});
            var Q6;
            Q6=makeQuery(id+"F15.opExtrude","SWEPT_BODY",BODY,{"disambiguationData":[OSD([sQuery(id+"F14.wireOp",EDGE,"E122"),sQuery(id+"F14.wireOp",EDGE,"E123"),sQuery(id+"F14.wireOp",EDGE,"E124"),sQuery(id+"F14.wireOp",EDGE,"E125"),sQuery(id+"F14.wireOp",EDGE,"E126"),sQuery(id+"F14.wireOp",EDGE,"E127"),sQuery(id+"F14.wireOp",EDGE,"E128"),sQuery(id+"F14.wireOp",EDGE,"E129"),sQuery(id+"F14.wireOp",EDGE,"E130"),sQuery(id+"F14.wireOp",EDGE,"E131"),sQuery(id+"F14.wireOp",EDGE,"E132"),sQuery(id+"F14.wireOp",EDGE,"E133"),sQuery(id+"F14.wireOp",EDGE,"E134"),sQuery(id+"F14.wireOp",EDGE,"E135")])]});
            var Q7;
            Q7 = qCreatedBy(id + "F17" ,VERTEX);
            var Q8;
            Q8=sQuery(id+"F14.wireOp",EDGE,"E156");
            transform(context, id + "F18", {"entities" : qUnion([Q0, Q1, Q2, Q3, Q4, Q5, Q6]), "transformType" : TransformType.TRANSLATION_ENTITY, "oppositeDirectionEntity" : false, "transformLine" : qUnion([Q7, Q8]), "makeCopy" : false});
        }
    });
